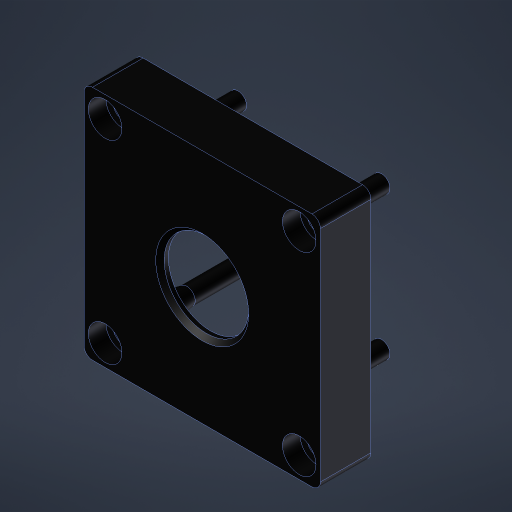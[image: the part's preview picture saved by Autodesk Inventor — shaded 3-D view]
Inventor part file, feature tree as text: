
AUTODESK INVENTOR PART (.ipt)
format: ipt  version: 2023 (Build 270158000, 158)  size: 388,096 bytes
history: native  units: in
note: dims shown in document units (in); Inventor stores cm internally (conversion verified against a paired STEP export)
features: sketch x6, hole x3, other x2, extrude x2, fillet x2, chamfer x2, shell x1, revolve x1
ambient origin geometry x8: Origin, YZ Plane, XZ Plane, XY Plane, X Axis, Y Axis, Z Axis, Center Point
bodies: Solid1 (feature_tree)
feature tree (19):
  other  "ELP Camera Case.ipt"
  sketch  "Sketch2"  dims[d10=0.0787in d11=0.0787in]
  extrude  "Extrusion1"  Depth=0.3937in TaperAngle=0.0deg
  hole  "Hole4"  [1 undecoded]
  shell  "Shell1"  Thickness=0.0394in
  fillet  "Fillet1"  Radius=0.3779in
  extrude  "Extrusion2"  TaperAngle=90.0deg  [1 undecoded]
  hole  "Hole2"  [1 undecoded]
  chamfer  "Chamfer1"  [1 undecoded]
  hole  "Hole3"  [1 undecoded]
  chamfer  "Chamfer2"  [1 undecoded]
  fillet  "Fillet2"  [1 undecoded]
  sketch  "Sketch1"  dims[d0=0.3937in d1=0.4724in d2=0.0in]
  sketch  "Sketch3"  dims[d12=0.4724in d13=0.5315in d14=0.0in d15=0.0in]
  sketch  "Sketch4"  dims[d16=0.0827in d17=0.2362in d18=0.1575in d19=0.0787in d20=90.0deg d21=0.0787in d22=0.0in]
  sketch  "Sketch5"  dims[d23=0.0787in d24=0.0787in d25=0.5497in]
  other  "Srf1"
  sketch  "Sketch6"  dims[d26=0.7874in d27=0.2362in d28=0.1575in d29=0.0787in d30=90.0deg d31=0.0787in d32=0.0in d33=0.0394in d34=0.0787in d35=0.5497in d36=0.3779in d37=90.0deg d38=0.177in d39=0.2362in d40=0.3125in d41=0.164in d42=0.5635in d43=0.315in d44=0.8108in d45=0.0394in d46=0.0in d47=0.0in d48=0.0in]
  revolve  "RevolutionSrf1"  [1 undecoded]
note: 8 required parameter values undecoded (feature->parameter linkage not recoverable at this tier; creation-order binding heuristic only, values carry confidence <= 0.55)
